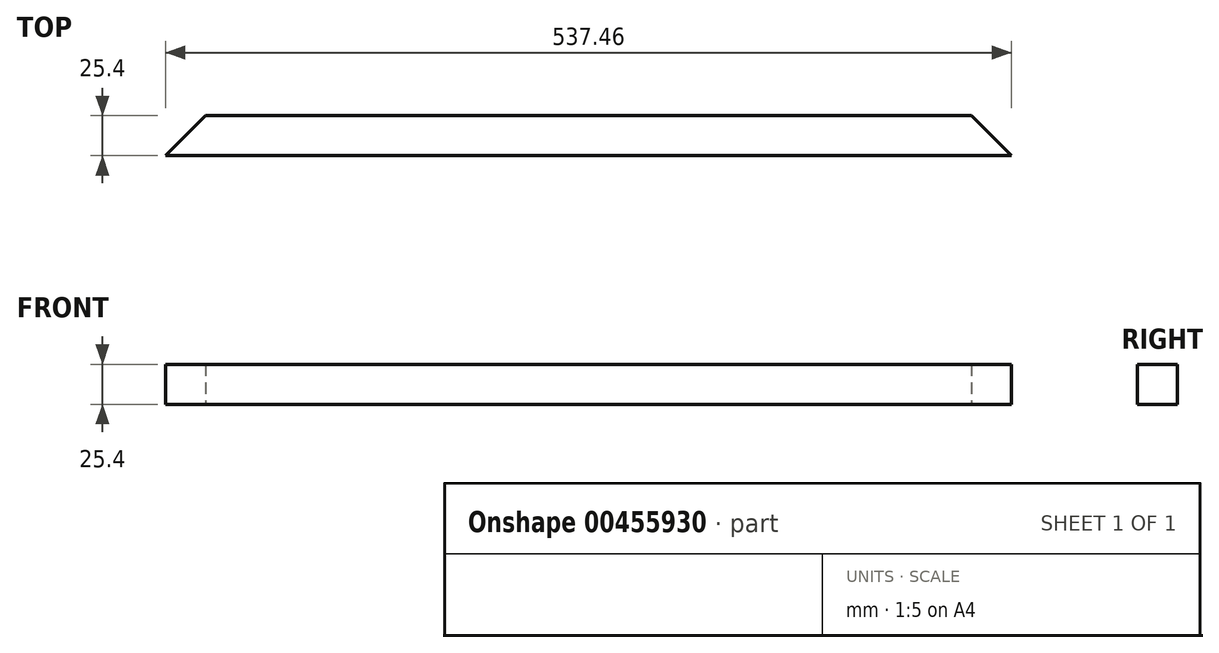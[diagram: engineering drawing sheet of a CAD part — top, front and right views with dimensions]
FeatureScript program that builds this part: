
annotation { "Feature Type Name" : "Feature", "Feature Type Description" : "" }
export const myFeature = defineFeature(function(context is Context, id is Id, definition is map)
    precondition{}
    {
        {
            var Q0;
            Q0=qCreatedBy(makeId("Top.planeOp"),FACE);
            var sketch = newSketch(context, id + "F0", { "sketchPlane" : qUnion([Q0])});
            skLineSegment(sketch, "E0.bottom", {"start": v(-268.73, 12.7) * mm, "end": v(268.73, 12.7) * mm});
            skLineSegment(sketch, "E0.top", {"start": v(-268.73, -12.7) * mm, "end": v(268.73, -12.7) * mm});
            skLineSegment(sketch, "E0.left", {"start": v(-268.73, 12.7) * mm, "end": v(-268.73, -12.7) * mm});
            skLineSegment(sketch, "E0.right", {"start": v(268.73, 12.7) * mm, "end": v(268.73, -12.7) * mm});
            skPoint(sketch, "E0.middle", {"position": v(0, 0) * mm});
            skLineSegment(sketch, "E1", {"start": v(-268.73, -12.7) * mm, "end": v(-243.33, 12.7) * mm});
            skLineSegment(sketch, "E2.MirrorCS", {"start": v(268.73, -12.7) * mm, "end": v(243.33, 12.7) * mm});
            skSolve(sketch);
        }
        {
            var Q0;
            Q0=makeQuery(id+"F0.imprint","IMPRINT",FACE,{"disambiguationData":[TD([[makeQuery(id+"F0.imprint","IMPRINT",EDGE,{"derivedFrom":sQuery(id+"F0.wireOp",EDGE,"E0.top")}),1.0]])]});
            extrude(context, id + "F1", {"entities" : qUnion([Q0]), "depth" : 25.4 * mm});
        }
    });
